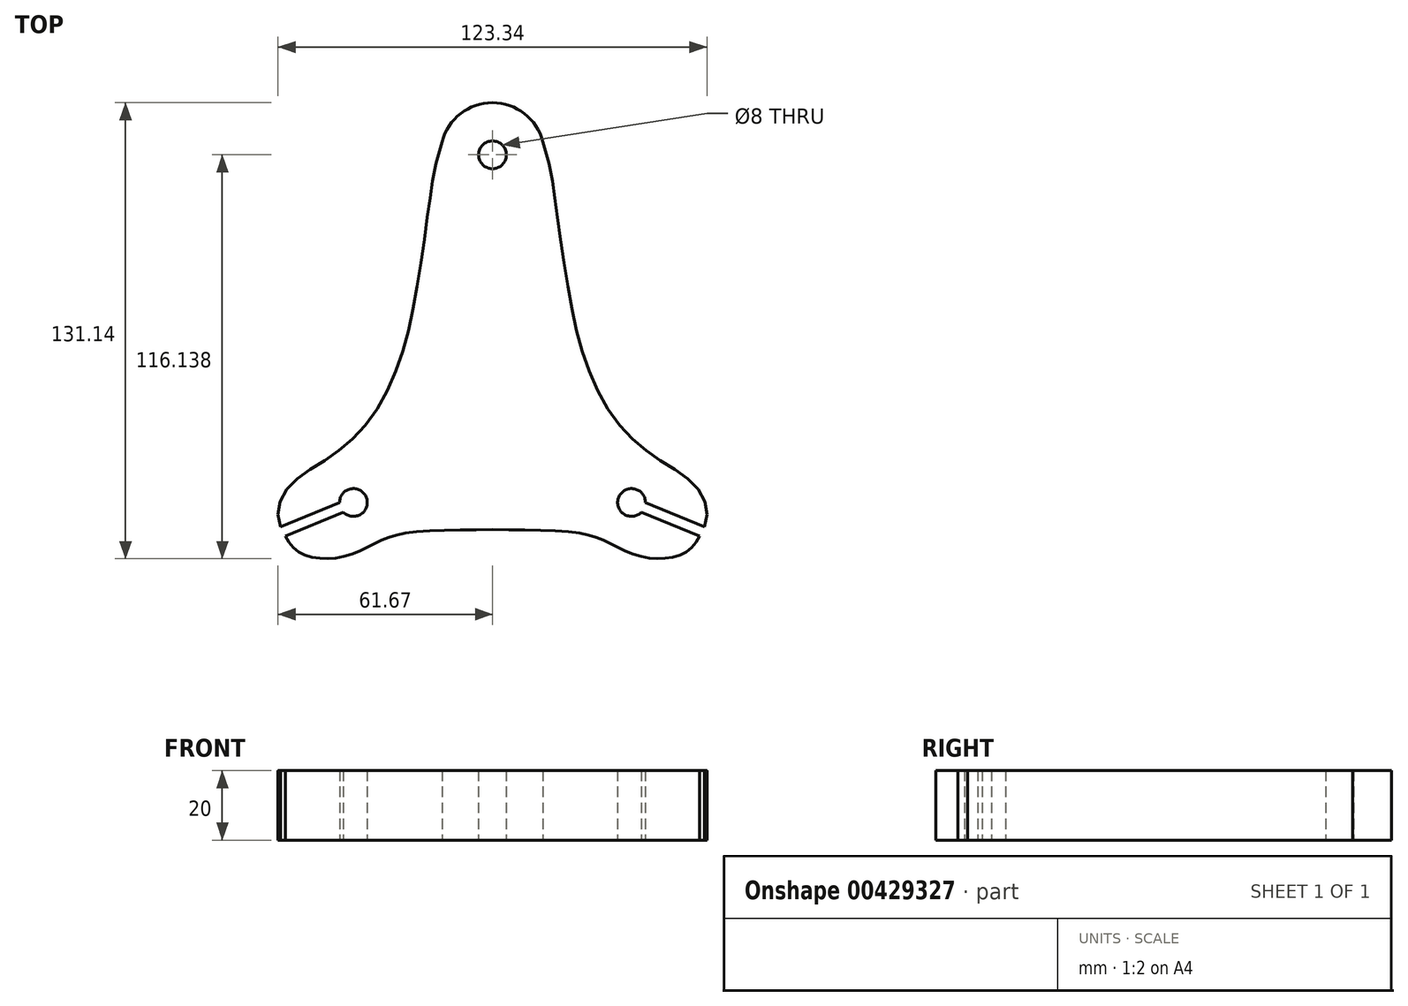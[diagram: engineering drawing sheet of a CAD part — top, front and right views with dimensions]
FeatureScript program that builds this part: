
annotation { "Feature Type Name" : "Feature", "Feature Type Description" : "" }
export const myFeature = defineFeature(function(context is Context, id is Id, definition is map)
    precondition{}
    {
        {
            var Q0;
            Q0=qCreatedBy(makeId("Top.planeOp"),FACE);
            var sketch = newSketch(context, id + "F0", { "sketchPlane" : qUnion([Q0])});
            skArc(sketch, "E0", {"start": v(14.51, 60.73) * mm, "mid": v(0, 71.94) * mm, "end": v(-14.51, 60.73) * mm});
            skLineSegment(sketch, "E1", {"start": v(0, 56.94) * mm, "end": v(0, -43.06) * mm, "construction": true});
            skLineSegment(sketch, "E2", {"start": v(0, -43.06) * mm, "end": v(100, -43.06) * mm, "construction": true});
            skLineSegment(sketch, "E3", {"start": v(0, -43.06) * mm, "end": v(-100, -43.06) * mm, "construction": true});
            skCircle(sketch, "E4", {"center": v(0, 56.94) * mm, "radius": 4 * mm});
            skArc(sketch, "E5", {"start": v(44, -43.09) * mm, "mid": v(36.3, -41.54) * mm, "end": v(42.86, -45.86) * mm});
            skFitSpline(sketch, "E6", {"points": [v(14.51, 60.73) * mm, v(18.1, 43.53) * mm, v(21.62, 19.4) * mm, v(26.92, -2.98) * mm, v(36.74, -21.04) * mm, v(48.56, -31.16) * mm, v(58.4, -38.28) * mm, v(61.67, -46.45) * mm, v(59.33, -53.22) * mm, v(55.5, -57.52) * mm, v(48.7, -59.19) * mm, v(40.92, -58.08) * mm, v(33.01, -54.47) * mm, v(25.52, -51.97) * mm, v(0, -50.88) * mm], "startDerivative": vector(82.25, -278.71) * mm, "endDerivative": vector(-284.94, 0) * mm});
            skLineSegment(sketch, "E7", {"start": v(40, -43.06) * mm, "end": v(60.31, -51.42) * mm, "construction": true});
            skLineSegment(sketch, "E8", {"start": v(44, -43.09) * mm, "end": v(60.91, -50.05) * mm});
            skLineSegment(sketch, "E9.MirrorCS", {"start": v(42.86, -45.86) * mm, "end": v(59.6, -52.75) * mm});
            skFitSpline(sketch, "E10.MirrorCS", {"points": [v(-14.51, 60.73) * mm, v(-18.1, 43.53) * mm, v(-21.62, 19.4) * mm, v(-26.92, -2.98) * mm, v(-36.74, -21.04) * mm, v(-48.56, -31.16) * mm, v(-58.4, -38.28) * mm, v(-61.67, -46.45) * mm, v(-59.33, -53.22) * mm, v(-55.5, -57.52) * mm, v(-48.7, -59.19) * mm, v(-40.92, -58.08) * mm, v(-33.01, -54.47) * mm, v(-25.52, -51.97) * mm, v(0, -50.88) * mm], "startDerivative": vector(-82.25, -278.71) * mm, "endDerivative": vector(284.94, 0) * mm});
            skArc(sketch, "E11.MirrorC", {"start": v(-44, -43.09) * mm, "mid": v(-36.3, -41.54) * mm, "end": v(-42.86, -45.86) * mm});
            skLineSegment(sketch, "E12.MirrorCS", {"start": v(-44, -43.09) * mm, "end": v(-60.91, -50.05) * mm});
            skLineSegment(sketch, "E13.MirrorCS", {"start": v(-40, -43.06) * mm, "end": v(-60.31, -51.42) * mm, "construction": true});
            skLineSegment(sketch, "E14.MirrorCS", {"start": v(-42.86, -45.86) * mm, "end": v(-59.6, -52.75) * mm});
            skPoint(sketch, "E15.orphan", {"position": v(59.77, -52.82) * mm});
            skPoint(sketch, "E16.orphan", {"position": v(-59.77, -52.82) * mm});
            skSolve(sketch);
        }
        {
            var Q0;
            {var subQ7=sQuery(id+"F0.wireOp",EDGE,"mxdsx3DX-6X0f-UorB-YDkH-IGln4bmSDeld");Q0=makeQuery(id+"F0.imprint","IMPRINT",FACE,{"disambiguationData":[TD([[makeQuery(id+"F0.imprint","IMPRINT",EDGE,{"derivedFrom":subQ7}),1.0]])]});}
            var Q1;
            Q1=makeQuery(id+"F0.imprint","IMPRINT",FACE,{"disambiguationData":[TD([[makeQuery(id+"F0.imprint","IMPRINT",EDGE,{"derivedFrom":sQuery(id+"F0.wireOp",EDGE,"E4")}),-1.0]])]});
            extrude(context, id + "F1", {"entities" : qUnion([Q0, Q1]), "depth" : 20 * mm, "offsetDistance" : 25 * mm});
        }
    });
